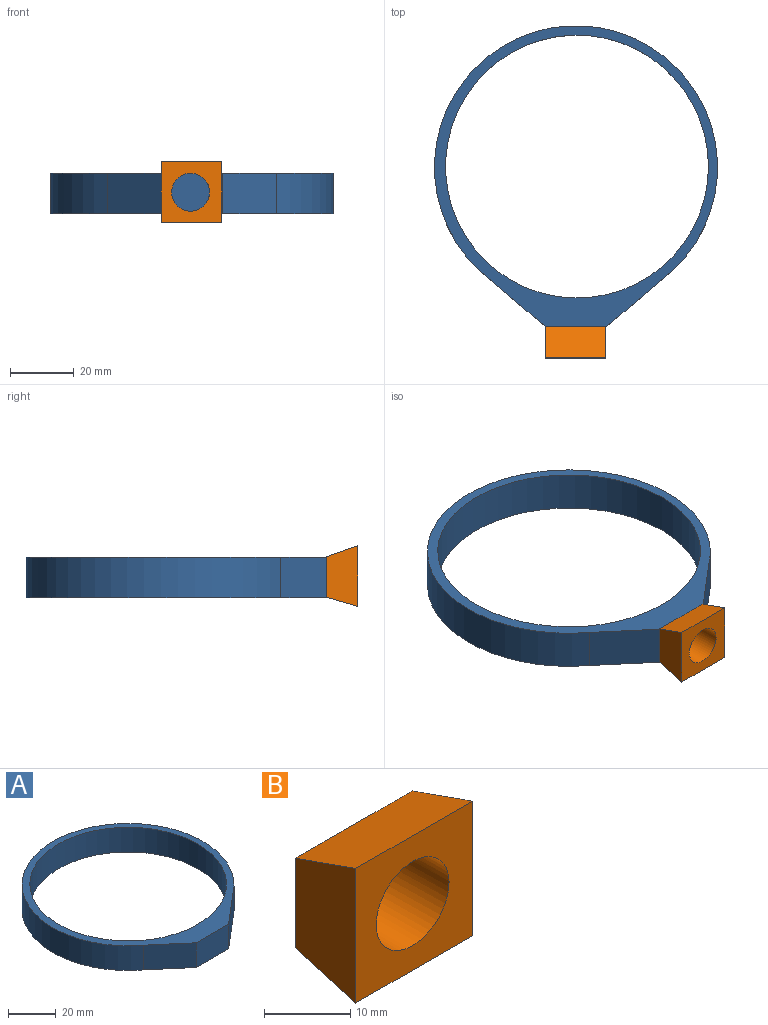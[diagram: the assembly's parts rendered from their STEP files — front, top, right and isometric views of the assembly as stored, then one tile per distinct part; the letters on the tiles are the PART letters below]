
ASSEMBLY  parts=2 mates=1
PART A: 7 faces, bbox 88.9x94.5x12.7 mm
  f0: cylinder r=44.45mm len=88.9mm, axis (0,0,-1), area 2824.8mm2, adj f1,f3,f5,f6
  f1: plane 16.86x14.37mm, normal (-0.65,-0.76,0), area 281.4mm2, adj f0,f2,f5,f6
  f2: plane 19.33x12.7mm, normal (0,-1,0), area 245.5mm2, adj f1,f3,f5,f6
  f3: plane 16.86x14.37mm, normal (0.65,-0.76,0), area 281.4mm2, adj f0,f2,f5,f6
  f4: cylinder r=41.27mm len=82.55mm, axis (0,0,-1), area 3293.6mm2, adj f5,f6
  f5: plane 94.48x88.9mm, normal (0,0,1), area 1057.7mm2, adj f0,f1,f2,f3,f4
  f6: plane 94.48x88.9mm, normal (0,0,-1), area 1057.7mm2, adj f0,f1,f2,f3,f4
PART B: 7 faces, bbox 19.1x9.8x19.1 mm
  f0: plane 19.05x19.05mm, normal (0,-1,0), area 251.4mm2, adj f1,f3,f4,f5,f6
  f1: plane 19.05x9.84mm, normal (0,0.28,-0.96), area 195.3mm2, adj f0,f2,f4,f5
  f2: plane 19.05x12.7mm, normal (0,1,0), area 130.5mm2, adj f1,f3,f4,f5,f6
  f3: plane 19.05x9.84mm, normal (0,0.33,0.94), area 198.9mm2, adj f0,f2,f4,f5
  f4: plane 19.05x9.84mm, normal (1,0,0), area 156.3mm2, adj f0,f1,f2,f3
  f5: plane 19.05x9.84mm, normal (-1,0,0), area 156.3mm2, adj f0,f1,f2,f3
  f6: cylinder r=5.96mm len=11.91mm, axis (0,-1,0), area 368.4mm2, adj f0,f2
PLACE A t=(19.97,-0.56,12.39)mm
PLACE B t=(10.24,-28.58,9.69)mm
MATE fastened A.f2 <-> B.f2  axis (0,-1,0) through (19.97,-18.74,18.74)mm
